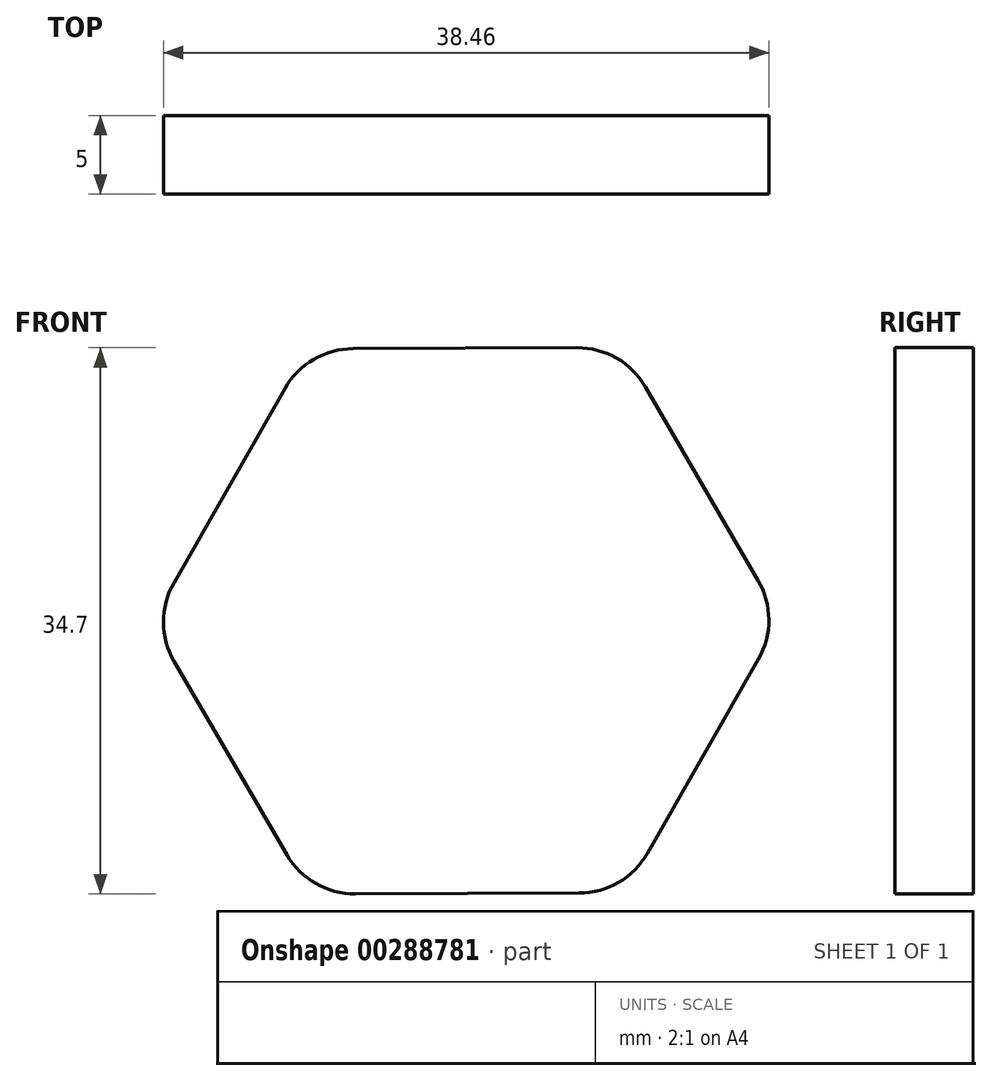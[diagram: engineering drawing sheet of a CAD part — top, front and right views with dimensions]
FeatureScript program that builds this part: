
annotation { "Feature Type Name" : "Feature", "Feature Type Description" : "" }
export const myFeature = defineFeature(function(context is Context, id is Id, definition is map)
    precondition{}
    {
        {
            var Q0;
            Q0=qCreatedBy(makeId("Front.planeOp"),FACE);
            var sketch = newSketch(context, id + "F0", { "sketchPlane" : qUnion([Q0])});
            skLineSegment(sketch, "E0.0", {"start": v(11.38, 14.87) * mm, "end": v(18.55, 2.58) * mm});
            skLineSegment(sketch, "E0.1", {"start": v(18.57, -2.42) * mm, "end": v(11.5, -14.77) * mm});
            skLineSegment(sketch, "E0.2", {"start": v(7.19, -17.3) * mm, "end": v(-7.04, -17.35) * mm});
            skLineSegment(sketch, "E0.3", {"start": v(-11.38, -14.87) * mm, "end": v(-18.55, -2.58) * mm});
            skLineSegment(sketch, "E0.4", {"start": v(-18.57, 2.42) * mm, "end": v(-11.5, 14.77) * mm});
            skLineSegment(sketch, "E0.5", {"start": v(-7.19, 17.3) * mm, "end": v(7.04, 17.35) * mm});
            skPoint(sketch, "E1.visualSharp", {"position": v(-20, -0.08) * mm});
            skArc(sketch, "E1.filletArc", {"start": v(-18.57, 2.42) * mm, "mid": v(-19.23, -0.08) * mm, "end": v(-18.55, -2.58) * mm});
            skPoint(sketch, "E2.visualSharp", {"position": v(20, 0.08) * mm});
            skArc(sketch, "E2.filletArc", {"start": v(18.57, -2.42) * mm, "mid": v(19.23, 0.08) * mm, "end": v(18.55, 2.58) * mm});
            skPoint(sketch, "E3.visualSharp", {"position": v(9.93, 17.36) * mm});
            skArc(sketch, "E3.filletArc", {"start": v(11.38, 14.87) * mm, "mid": v(9.54, 16.7) * mm, "end": v(7.04, 17.35) * mm});
            skPoint(sketch, "E4.visualSharp", {"position": v(-10.07, 17.28) * mm});
            skArc(sketch, "E4.filletArc", {"start": v(-7.19, 17.3) * mm, "mid": v(-9.68, 16.61) * mm, "end": v(-11.5, 14.77) * mm});
            skPoint(sketch, "E5.visualSharp", {"position": v(10.07, -17.28) * mm});
            skArc(sketch, "E5.filletArc", {"start": v(7.19, -17.3) * mm, "mid": v(9.68, -16.61) * mm, "end": v(11.5, -14.77) * mm});
            skPoint(sketch, "E6.visualSharp", {"position": v(-9.93, -17.36) * mm});
            skArc(sketch, "E6.filletArc", {"start": v(-11.38, -14.87) * mm, "mid": v(-9.54, -16.7) * mm, "end": v(-7.04, -17.35) * mm});
            skSolve(sketch);
        }
        {
            var Q0;
            Q0=makeQuery(id+"F0.imprint","IMPRINT",FACE,{"disambiguationData":[TD([[makeQuery(id+"F0.imprint","IMPRINT",EDGE,{"derivedFrom":sQuery(id+"F0.wireOp",EDGE,"E0.0")}),-1.0]])]});
            extrude(context, id + "F1", {"entities" : qUnion([Q0]), "depth" : 5 * mm});
        }
    });
